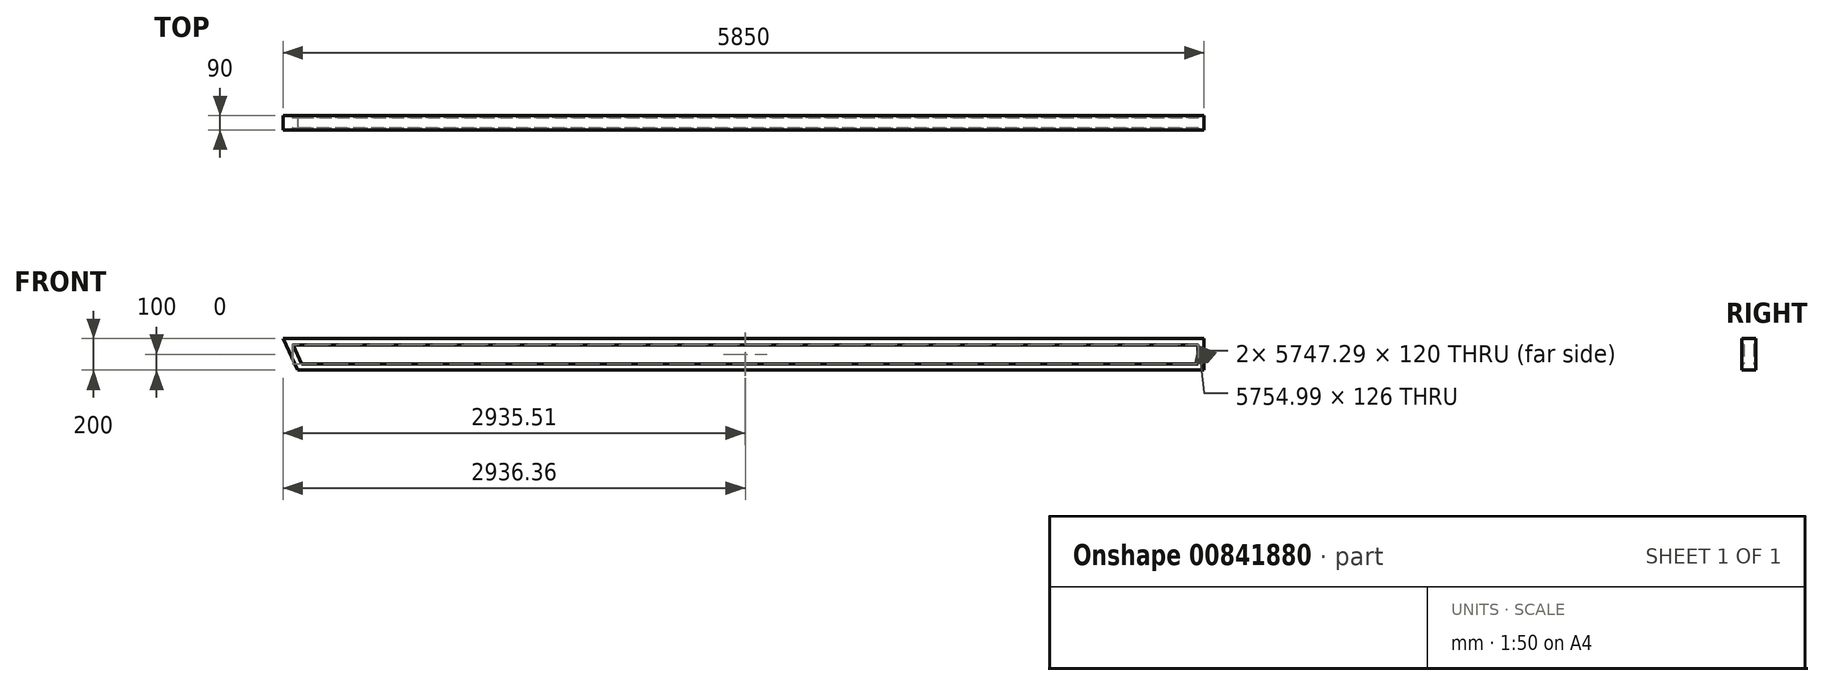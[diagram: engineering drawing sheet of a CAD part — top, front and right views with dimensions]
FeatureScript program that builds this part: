
annotation { "Feature Type Name" : "Feature", "Feature Type Description" : "" }
export const myFeature = defineFeature(function(context is Context, id is Id, definition is map)
    precondition{}
    {
        {
            var Q0;
            Q0=qCreatedBy(makeId("Front.planeOp"),FACE);
            var sketch = newSketch(context, id + "F0", { "sketchPlane" : qUnion([Q0])});
            skLineSegment(sketch, "E0.bottom", {"start": v(0, 0) * mm, "end": v(5757, 0) * mm});
            skLineSegment(sketch, "E0.top", {"start": v(-93, 200) * mm, "end": v(5757, 200) * mm});
            skLineSegment(sketch, "E0.right", {"start": v(5757, 0) * mm, "end": v(5757, 200) * mm});
            skLineSegment(sketch, "E1", {"start": v(-93, 200) * mm, "end": v(0, 0) * mm});
            skPoint(sketch, "E2.orphan", {"position": v(-93, 0) * mm});
            skSolve(sketch);
        }
        {
            var Q0;
            Q0=qCreatedBy(makeId("Right.planeOp"),FACE);
            var sketch = newSketch(context, id + "F1", { "sketchPlane" : qUnion([Q0])});
            skLineSegment(sketch, "E3", {"start": v(0, 0) * mm, "end": v(-45, 0) * mm});
            skLineSegment(sketch, "E4", {"start": v(-45, 0) * mm, "end": v(-45, 40) * mm});
            skLineSegment(sketch, "E5", {"start": v(-45, 40) * mm, "end": v(-33, 40) * mm});
            skLineSegment(sketch, "E6.MirrorCS", {"start": v(45, 40) * mm, "end": v(33, 40) * mm});
            skLineSegment(sketch, "E7.MirrorCS", {"start": v(45, 0) * mm, "end": v(45, 40) * mm});
            skLineSegment(sketch, "E8.MirrorCS", {"start": v(0, 0) * mm, "end": v(45, 0) * mm});
            skLineSegment(sketch, "E9.0", {"start": v(-42, 37) * mm, "end": v(-33, 37) * mm});
            skLineSegment(sketch, "E9.1", {"start": v(-42, 3) * mm, "end": v(-42, 37) * mm});
            skLineSegment(sketch, "E9.2", {"start": v(42, 37) * mm, "end": v(33, 37) * mm});
            skLineSegment(sketch, "E9.3", {"start": v(42, 3) * mm, "end": v(42, 37) * mm});
            skLineSegment(sketch, "E9.4", {"start": v(0, 3) * mm, "end": v(42, 3) * mm});
            skLineSegment(sketch, "E9.5", {"start": v(0, 3) * mm, "end": v(-42, 3) * mm});
            skLineSegment(sketch, "E10", {"start": v(33, 40) * mm, "end": v(33, 37) * mm});
            skLineSegment(sketch, "E11", {"start": v(-33, 40) * mm, "end": v(-33, 37) * mm});
            skSolve(sketch);
        }
        {
            var Q0;
            Q0=qSketchRegion(id+"F1",true);
            var Q1;
            Q1=qConstructionFilter(qBodyType(qCreatedBy(id+"F0",EDGE),BodyType.WIRE),ConstructionObject.NO);
            sweep(context, id + "F2", {"profiles" : qUnion([Q0]), "path" : qUnion([Q1])});
        }
    });
